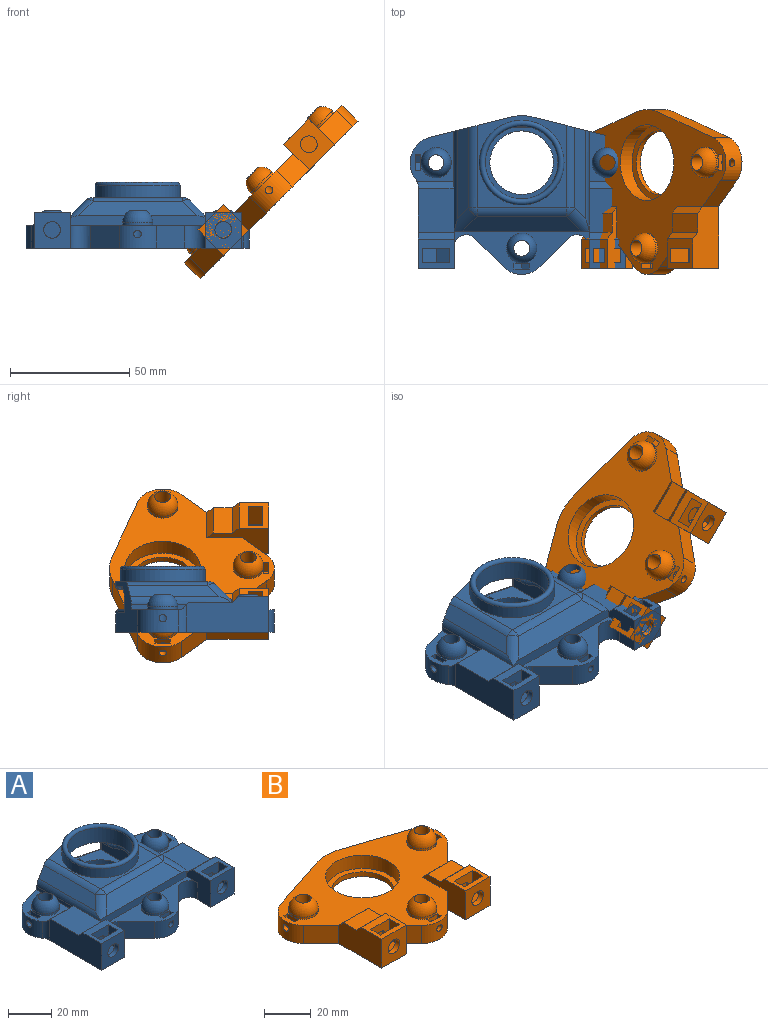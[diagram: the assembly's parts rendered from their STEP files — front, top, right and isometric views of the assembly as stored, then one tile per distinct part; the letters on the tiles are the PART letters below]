
ASSEMBLY  parts=2 mates=1
PART A: 137 faces, bbox 94x68.5x27.9 mm
  f0: plane 56.57x18.14mm, normal (0,0,1), area 376.9mm2, adj f1,f16,f17,f18,f32,f33,f34,f35
  f1: plane 56.98x4.44mm, normal (0,-1,0), area 230.6mm2, adj f0,f2,f5,f64,f65,f110,f113,f118
  f2: cylinder r=5.08mm len=42.23mm, axis (0,1,0), area 145.4mm2, adj f1,f22,f65,f68,f96,f111,f113
  f3: plane 21.1x18.45mm, normal (0,0,1), area 182.4mm2, adj f4,f11,f13,f40,f41,f42,f43,f52
  f4: plane 23.11x2.01mm, normal (-1,0,0), area 44.4mm2, adj f3,f5,f13,f69
  f5: cylinder r=5.08mm len=42.23mm, axis (0,-1,0), area 145.4mm2, adj f1,f4,f13,f64,f69,f109,f118
  f6: plane 22.5x8.14mm, normal (0,0,-1), area 85.2mm2, adj f100,f103,f108,f122,f124,f126
  f7: plane 34.42x31.06mm, normal (0,0,1), area 448.5mm2, adj f25,f28,f29,f30,f31,f95,f97,f98
  f8: plane 15.14x12.4mm, normal (0,0,1), area 120.2mm2, adj f14,f15,f67,f75,f76,f77,f78,f133
  f9: plane 15.14x12.4mm, normal (0,0,1), area 120.2mm2, adj f19,f20,f66,f70,f71,f72,f73,f136
  f10: plane 21.1x18.45mm, normal (0,0,1), area 182.4mm2, adj f21,f22,f36,f37,f38,f39,f53,f68
  f11: cylinder r=10.92mm len=17.33mm, axis (0,0,-1), area 199mm2, adj f3,f13,f27,f61,f91
  f12: cylinder r=3.3mm len=15.88mm, axis (0,0,-1), area 321.2mm2, adj f27,f57,f60
  f13: plane 33.96x21.44mm, normal (-0.24,0.97,0), area 452.5mm2, adj f3,f4,f5,f11,f26,f27,f99,f101
  f14: plane 34.54x15.19mm, normal (-1,0,0), area 465.8mm2, adj f8,f15,f27,f64,f67,f69,f91
  f15: plane 15.19x15.14mm, normal (0,-1,0), area 191.3mm2, adj f8,f14,f27,f83,f133
  f16: plane 11.93x11.93mm, normal (-0.71,-0.71,0), area 160.7mm2, adj f0,f17,f27,f89
  f17: cylinder r=10.92mm len=15.45mm, axis (0,0,-1), area 155.5mm2, adj f0,f16,f18,f27,f62
  f18: plane 11.93x11.93mm, normal (0.71,-0.71,0), area 160.7mm2, adj f0,f17,f27,f90
  f19: plane 15.19x15.14mm, normal (0,-1,0), area 191.3mm2, adj f9,f20,f27,f86,f136
  f20: plane 34.54x15.19mm, normal (1,0,0), area 465.8mm2, adj f9,f19,f27,f65,f66,f68,f92
  f21: cylinder r=10.92mm len=17.33mm, axis (0,0,-1), area 199mm2, adj f10,f22,f27,f59,f92
  f22: plane 33.96x21.44mm, normal (0.24,0.97,0), area 452.5mm2, adj f2,f10,f21,f26,f27,f96,f99,f101
  f23: cylinder r=3.3mm len=15.88mm, axis (0,0,-1), area 322.7mm2, adj f27,f55,f58
  f24: cylinder r=3.3mm len=15.88mm, axis (0,0,-1), area 321.2mm2, adj f27,f56,f63
  f25: cylinder r=13.33mm len=26.67mm, axis (0,0,-1), area 790.1mm2, adj f7,f27,f93
  f26: cylinder r=19.69mm len=9.6mm, axis (0,0,-1), area 72.2mm2, adj f13,f22,f27,f94,f123
  f27: plane 93.69x66.53mm, normal (0,0,-1), area 4184.5mm2, adj f11,f12,f13,f14,f15,f16,f17,f18
  f28: plane 5.46x2.34mm, normal (-1,0,0), area 12.8mm2, adj f7,f29,f31,f45
  f29: plane 7.32x6.45mm, normal (0,-1,0), area 33.3mm2, adj f7,f28,f30,f44,f45,f94
  f30: plane 5.46x2.34mm, normal (1,0,0), area 12.8mm2, adj f7,f29,f31,f44
  f31: plane 7.32x6.45mm, normal (0,1,0), area 33.3mm2, adj f7,f28,f30,f44,f45,f93
  f32: plane 7.32x6.45mm, normal (0,-1,0), area 33.3mm2, adj f0,f33,f35,f48,f49,f63
  f33: plane 5.46x2.34mm, normal (1,0,0), area 12.8mm2, adj f0,f32,f34,f49
  f34: plane 7.32x6.45mm, normal (0,1,0), area 33.3mm2, adj f0,f33,f35,f48,f49,f62
  f35: plane 5.46x2.34mm, normal (-1,0,0), area 12.8mm2, adj f0,f32,f34,f48
  f36: plane 5.46x2.34mm, normal (0,1,0), area 12.8mm2, adj f10,f37,f39,f47
  f37: plane 7.32x6.45mm, normal (-1,0,0), area 33.3mm2, adj f10,f36,f38,f46,f47,f59
  f38: plane 5.46x2.34mm, normal (0,-1,0), area 12.8mm2, adj f10,f37,f39,f46
  f39: plane 7.32x6.45mm, normal (1,0,0), area 33.3mm2, adj f10,f36,f38,f46,f47,f58
  f40: plane 5.46x2.34mm, normal (0,-1,0), area 12.8mm2, adj f3,f41,f43,f50
  f41: plane 7.32x6.45mm, normal (1,0,0), area 33.3mm2, adj f3,f40,f42,f50,f51,f61
  f42: plane 5.46x2.34mm, normal (0,1,0), area 12.8mm2, adj f3,f41,f43,f51
  f43: plane 7.32x6.45mm, normal (-1,0,0), area 33.3mm2, adj f3,f40,f42,f50,f51,f60
  f44: plane 3.23x2.34mm, normal (0.5,0,0.87), area 8.7mm2, adj f29,f30,f31,f45
  f45: plane 3.23x2.34mm, normal (-0.5,0,0.87), area 8.7mm2, adj f28,f29,f31,f44
  f46: plane 3.23x2.34mm, normal (0,-0.5,0.87), area 8.7mm2, adj f37,f38,f39,f47
  f47: plane 3.23x2.34mm, normal (0,0.5,0.87), area 8.7mm2, adj f36,f37,f39,f46
  f48: plane 3.23x2.34mm, normal (-0.5,0,0.87), area 8.7mm2, adj f32,f34,f35,f49
  f49: plane 3.23x2.34mm, normal (0.5,0,0.87), area 8.7mm2, adj f32,f33,f34,f48
  f50: plane 3.23x2.34mm, normal (0,-0.5,0.87), area 8.7mm2, adj f40,f41,f43,f51
  f51: plane 3.23x2.34mm, normal (0,0.5,0.87), area 8.7mm2, adj f41,f42,f43,f50
  f52: cylinder r=6.35mm len=12.7mm, axis (0,0,-1), area 42.7mm2, adj f3,f57
  f53: cylinder r=6.35mm len=12.7mm, axis (0,0,-1), area 42.7mm2, adj f10,f55
  f54: cylinder r=6.35mm len=12.7mm, axis (0,0,-1), area 42.7mm2, adj f0,f56
  f55: torus R=0.25mm, axis (0,0,1), area 212.4mm2, adj f23,f53
  f56: torus R=0.25mm, axis (0,0,1), area 212.4mm2, adj f24,f54
  f57: torus R=0.25mm, axis (0,0,1), area 212.4mm2, adj f12,f52
  f58: cylinder r=1.59mm len=3.49mm, axis (-1,0,0), area 31.5mm2, adj f23,f39
  f59: cylinder r=1.59mm len=3.18mm, axis (-1,0,0), area 21.1mm2, adj f21,f37
  f60: cylinder r=1.59mm len=3.18mm, axis (-1,0,0), area 30.4mm2, adj f12,f43
  f61: cylinder r=1.59mm len=3.18mm, axis (-1,0,0), area 22.3mm2, adj f11,f41
  f62: cylinder r=1.59mm len=3.18mm, axis (0,1,0), area 21.1mm2, adj f17,f34
  f63: cylinder r=1.59mm len=3.49mm, axis (0,1,0), area 34.8mm2, adj f24,f32
  f64: plane 18.44x15.14mm, normal (0,0,1), area 278.4mm2, adj f1,f5,f14,f67,f69,f133
  f65: plane 18.44x15.14mm, normal (0,0,1), area 278.4mm2, adj f1,f2,f20,f66,f68,f136
  f66: plane 15.14x2.82mm, normal (0,0.71,0.71), area 60.4mm2, adj f9,f20,f65,f136
  f67: plane 15.14x2.82mm, normal (0,0.71,0.71), area 60.4mm2, adj f8,f14,f64,f133
  f68: plane 15.52x2.88mm, normal (0,0.71,0.71), area 60.8mm2, adj f2,f10,f20,f65,f92,f96
  f69: plane 15.52x2.88mm, normal (0,0.71,0.71), area 60.8mm2, adj f3,f4,f5,f14,f64,f91
  f70: plane 14x11.25mm, normal (0,-1,0), area 100.6mm2, adj f9,f71,f73,f74,f79,f82,f87
  f71: plane 10.75x5.99mm, normal (1,0,0), area 64.5mm2, adj f9,f70,f72,f82
  f72: plane 14x11.25mm, normal (0,1,0), area 100.6mm2, adj f9,f71,f73,f74,f79,f82,f86
  f73: plane 10.74x5.99mm, normal (-1,0,0), area 64.4mm2, adj f9,f70,f72,f79
  f74: plane 5.99x0.01mm, normal (0,0,1), area 0mm2, adj f70,f72,f79,f82
  f75: plane 13.99x11.25mm, normal (0,-1,0), area 100.6mm2, adj f8,f76,f78,f80,f81,f84
  f76: plane 10.74x5.99mm, normal (1,0,0), area 64.4mm2, adj f8,f75,f77,f81
  f77: plane 13.99x11.25mm, normal (0,1,0), area 100.6mm2, adj f8,f76,f78,f80,f81,f83
  f78: plane 10.74x5.99mm, normal (-1,0,0), area 64.4mm2, adj f8,f75,f77,f80
  f79: plane 5.99x5.63mm, normal (-0.5,0,0.87), area 39mm2, adj f70,f72,f73,f74
  f80: plane 5.99x5.63mm, normal (-0.5,0,0.87), area 38.9mm2, adj f75,f77,f78,f81
  f81: plane 5.99x5.63mm, normal (0.5,0,0.87), area 38.9mm2, adj f75,f76,f77,f80
  f82: plane 5.99x5.61mm, normal (0.5,0,0.87), area 38.9mm2, adj f70,f71,f72,f74
  f83: cylinder r=3.51mm len=7.01mm, axis (0,1,0), area 54.8mm2, adj f15,f77
  f84: cylinder r=3.51mm len=7.01mm, axis (0,1,0), area 35.8mm2, adj f75,f85
  f85: plane 7.01x7.01mm, normal (0,-1,0), area 38.6mm2, adj f84
  f86: cylinder r=3.51mm len=7.01mm, axis (0,1,0), area 54.8mm2, adj f19,f72
  f87: cylinder r=3.51mm len=7.01mm, axis (0,1,0), area 35.8mm2, adj f70,f88
  f88: plane 7.01x7.01mm, normal (0,-1,0), area 38.6mm2, adj f87
  f89: cylinder r=5.13mm len=9.53mm, axis (0,0,1), area 115.1mm2, adj f0,f16,f27,f131,f132
  f90: cylinder r=5.13mm len=9.53mm, axis (0,0,1), area 115.1mm2, adj f0,f18,f27,f134,f135
  f91: cylinder r=5.13mm len=11.49mm, axis (0,0,-1), area 34.5mm2, adj f3,f11,f14,f27,f69
  f92: cylinder r=5.13mm len=11.49mm, axis (0,0,-1), area 34.5mm2, adj f10,f20,f21,f27,f68
  f93: cylinder r=1.59mm len=3.18mm, axis (0,1,0), area 13.7mm2, adj f25,f31
  f94: cylinder r=1.59mm len=3.18mm, axis (0,1,0), area 26.7mm2, adj f26,f29
  f95: plane 30.77x7.12mm, normal (1,0,0), area 158.5mm2, adj f7,f98,f106,f107,f108,f127
  f96: plane 23.11x2.01mm, normal (1,0,0), area 44.4mm2, adj f2,f10,f22,f68
  f97: plane 30.77x7.12mm, normal (-1,0,0), area 158.5mm2, adj f7,f98,f103,f104,f105,f119
  f98: plane 30.99x8.56mm, normal (0,1,0), area 257.5mm2, adj f7,f95,f97,f102,f105,f106
  f99: cylinder r=19.69mm len=9.6mm, axis (0,0,-1), area 18.5mm2, adj f13,f22,f101,f124
  f100: cylinder r=15.24mm len=30.48mm, axis (0,0,-1), area 790.5mm2, adj f6,f102,f104,f107,f130
  f101: plane 38.66x37.35mm, normal (0,0,1), area 384mm2, adj f13,f22,f99,f112,f115,f116,f129
  f102: plane 22.5x5.72mm, normal (0,0,-1), area 51.5mm2, adj f98,f100,f105,f106
  f103: cylinder r=4.24mm len=5.88mm, axis (0,1,0), area 34.6mm2, adj f6,f97,f104,f120
  f104: bspline ~20.56x4.24mm, area 73.7mm2, adj f97,f100,f103,f105
  f105: cylinder r=4.24mm len=5.72mm, axis (0,1,0), area 38.1mm2, adj f97,f98,f102,f104
  f106: cylinder r=4.24mm len=5.72mm, axis (0,-1,0), area 38.1mm2, adj f95,f98,f102,f107
  f107: bspline ~20.56x4.24mm, area 73.7mm2, adj f95,f100,f106,f108
  f108: cylinder r=4.24mm len=5.88mm, axis (0,-1,0), area 34.6mm2, adj f6,f95,f107,f128
  f109: plane 38.32x4.64mm, normal (-0.71,0,0.71), area 232.6mm2, adj f5,f13,f115,f118
  f110: plane 49.61x6.13mm, normal (0,-0.71,0.71), area 377mm2, adj f1,f113,f116,f118
  f111: plane 38.32x4.64mm, normal (0.71,0,0.71), area 232.6mm2, adj f2,f22,f112,f113
  f112: cylinder r=5.08mm len=34.58mm, axis (0,1,0), area 136.2mm2, adj f22,f101,f111,f114
  f113: cylinder r=5.08mm len=11.17mm, axis (0.58,-0.58,-0.58), area 59.6mm2, adj f1,f2,f110,f111,f114
  f114: sphere r=5.08mm, area 8.8mm2, adj f112,f113,f116
  f115: cylinder r=5.08mm len=34.58mm, axis (0,-1,0), area 136.2mm2, adj f13,f101,f109,f117
  f116: cylinder r=5.08mm len=37.35mm, axis (1,0,0), area 149mm2, adj f101,f110,f114,f117
  f117: sphere r=5.08mm, area 11.9mm2, adj f115,f116,f118
  f118: cylinder r=5.08mm len=11.17mm, axis (-0.58,-0.58,-0.58), area 59.6mm2, adj f1,f5,f109,f110,f117
  f119: cylinder r=1.27mm len=5.59mm, axis (0,0,-1), area 10.9mm2, adj f7,f22,f97,f120,f121
  f120: bspline ~6.01x5.75mm, area 16.3mm2, adj f22,f103,f119,f122
  f121: cylinder r=1.27mm len=12.58mm, axis (0.97,-0.24,0), area 24mm2, adj f7,f22,f119,f123
  f122: cylinder r=1.27mm len=7.07mm, axis (-0.97,0.24,0), area 13.9mm2, adj f6,f22,f120,f124
  f123: torus R=18.41mm, axis (0,0,1), area 18.9mm2, adj f7,f26,f121,f125
  f124: torus R=18.41mm, axis (0,0,1), area 18.9mm2, adj f6,f99,f122,f126
  f125: cylinder r=1.27mm len=12.58mm, axis (0.97,0.24,0), area 24mm2, adj f7,f13,f123,f127
  f126: cylinder r=1.27mm len=7.07mm, axis (-0.97,-0.24,0), area 13.9mm2, adj f6,f13,f124,f128
  f127: cylinder r=1.27mm len=5.59mm, axis (0,0,-1), area 10.9mm2, adj f7,f13,f95,f125,f128
  f128: bspline ~6.01x5.51mm, area 16.3mm2, adj f13,f108,f126,f127
  f129: cylinder r=17.78mm len=35.56mm, axis (0,0,-1), area 567.5mm2, adj f101,f130
  f130: torus R=16.51mm, axis (0,0,1), area 413.9mm2, adj f100,f129
  f131: plane 9.53x0.13mm, normal (0,1,0), area 1.2mm2, adj f27,f89,f132,f133
  f132: plane 1.13x0.13mm, normal (0,0,-1), area 0.1mm2, adj f89,f131,f133
  f133: plane 15.75x15.19mm, normal (1,0,0), area 170.5mm2, adj f0,f1,f8,f15,f27,f64,f67,f131
  f134: plane 1.13x0.13mm, normal (0,0,-1), area 0.1mm2, adj f90,f135,f136
  f135: plane 9.53x0.13mm, normal (0,1,0), area 1.2mm2, adj f27,f90,f134,f136
  f136: plane 15.75x15.19mm, normal (-1,0,0), area 170.5mm2, adj f0,f1,f9,f19,f27,f65,f66,f134
PART B: 81 faces, bbox 93.7x69.1x15.9 mm
  f0: plane 15.01x12.4mm, normal (0,0,1), area 118.6mm2, adj f7,f8,f9,f59,f67,f68,f69,f70
  f1: plane 15.01x12.4mm, normal (0,0,1), area 118.6mm2, adj f13,f14,f15,f58,f62,f63,f64,f65
  f2: plane 93.69x69.07mm, normal (0,0,1), area 2582.6mm2, adj f3,f5,f6,f9,f10,f11,f12,f13
  f3: cylinder r=10.92mm len=18.09mm, axis (0,0,-1), area 203.9mm2, adj f2,f5,f6,f23,f53
  f4: cylinder r=3.3mm len=15.88mm, axis (0,0,-1), area 321.2mm2, adj f23,f49,f52
  f5: plane 32.36x10.73mm, normal (-0.31,0.95,0), area 324.8mm2, adj f2,f3,f22,f23
  f6: plane 10.74x10.74mm, normal (-0.71,-0.71,0), area 144.7mm2, adj f2,f3,f7,f23
  f7: plane 25.99x15.19mm, normal (-1,0,0), area 356.3mm2, adj f0,f6,f8,f23,f56,f59,f61
  f8: plane 15.19x15.01mm, normal (0,-1,0), area 189.4mm2, adj f0,f7,f9,f23,f75
  f9: plane 25.99x15.19mm, normal (1,0,0), area 213.4mm2, adj f0,f2,f8,f10,f23,f56,f59,f61
  f10: plane 10.17x10.17mm, normal (-0.71,-0.71,0), area 137mm2, adj f2,f9,f11,f23
  f11: cylinder r=10.92mm len=15.45mm, axis (0,0,-1), area 155.5mm2, adj f2,f10,f12,f23,f54
  f12: plane 10.17x10.17mm, normal (0.71,-0.71,0), area 137mm2, adj f2,f11,f13,f23
  f13: plane 25.99x15.19mm, normal (-1,0,0), area 213.4mm2, adj f1,f2,f12,f14,f23,f57,f58,f60
  f14: plane 15.19x15.01mm, normal (0,-1,0), area 189.4mm2, adj f1,f13,f15,f23,f78
  f15: plane 25.99x15.19mm, normal (1,0,0), area 356.3mm2, adj f1,f14,f16,f23,f57,f58,f60
  f16: plane 10.74x10.74mm, normal (0.71,-0.71,0), area 144.7mm2, adj f2,f15,f17,f23
  f17: cylinder r=10.92mm len=18.09mm, axis (0,0,-1), area 203.9mm2, adj f2,f16,f18,f23,f51
  f18: plane 32.36x10.73mm, normal (0.31,0.95,0), area 324.8mm2, adj f2,f17,f22,f23
  f19: cylinder r=3.3mm len=15.88mm, axis (0,0,-1), area 321.2mm2, adj f23,f47,f50
  f20: cylinder r=3.3mm len=15.88mm, axis (0,0,-1), area 321.2mm2, adj f23,f48,f55
  f21: cylinder r=15.88mm len=31.75mm, axis (0,0,-1), area 696.7mm2, adj f2,f25
  f22: cylinder r=22.23mm len=13.99mm, axis (0,0,-1), area 135.5mm2, adj f2,f5,f18,f23
  f23: plane 93.69x69.07mm, normal (0,0,-1), area 3918.4mm2, adj f3,f4,f5,f6,f7,f8,f9,f10
  f24: cylinder r=13.33mm len=26.67mm, axis (0,0,-1), area 212.8mm2, adj f23,f25
  f25: plane 31.75x31.75mm, normal (0,0,1), area 233.1mm2, adj f21,f24
  f26: plane 7.32x6.45mm, normal (0,-1,0), area 33.3mm2, adj f2,f27,f29,f40,f41,f55
  f27: plane 5.46x2.34mm, normal (1,0,0), area 12.8mm2, adj f2,f26,f28,f41
  f28: plane 7.32x6.45mm, normal (0,1,0), area 33.3mm2, adj f2,f27,f29,f40,f41,f54
  f29: plane 5.46x2.34mm, normal (-1,0,0), area 12.8mm2, adj f2,f26,f28,f40
  f30: plane 5.46x2.34mm, normal (0,1,0), area 12.8mm2, adj f2,f31,f33,f39
  f31: plane 7.32x6.45mm, normal (-1,0,0), area 33.3mm2, adj f2,f30,f32,f38,f39,f51
  f32: plane 5.46x2.34mm, normal (0,-1,0), area 12.8mm2, adj f2,f31,f33,f38
  f33: plane 7.32x6.45mm, normal (1,0,0), area 33.3mm2, adj f2,f30,f32,f38,f39,f50
  f34: plane 5.46x2.34mm, normal (0,-1,0), area 12.8mm2, adj f2,f35,f37,f42
  f35: plane 7.32x6.45mm, normal (1,0,0), area 33.3mm2, adj f2,f34,f36,f42,f43,f53
  f36: plane 5.46x2.34mm, normal (0,1,0), area 12.8mm2, adj f2,f35,f37,f43
  f37: plane 7.32x6.45mm, normal (-1,0,0), area 33.3mm2, adj f2,f34,f36,f42,f43,f52
  f38: plane 3.23x2.34mm, normal (0,-0.5,0.87), area 8.7mm2, adj f31,f32,f33,f39
  f39: plane 3.23x2.34mm, normal (0,0.5,0.87), area 8.7mm2, adj f30,f31,f33,f38
  f40: plane 3.23x2.34mm, normal (-0.5,0,0.87), area 8.7mm2, adj f26,f28,f29,f41
  f41: plane 3.23x2.34mm, normal (0.5,0,0.87), area 8.7mm2, adj f26,f27,f28,f40
  f42: plane 3.23x2.34mm, normal (0,-0.5,0.87), area 8.7mm2, adj f34,f35,f37,f43
  f43: plane 3.23x2.34mm, normal (0,0.5,0.87), area 8.7mm2, adj f35,f36,f37,f42
  f44: cylinder r=6.35mm len=12.7mm, axis (0,0,-1), area 42.7mm2, adj f2,f49
  f45: cylinder r=6.35mm len=12.7mm, axis (0,0,-1), area 42.7mm2, adj f2,f47
  f46: cylinder r=6.35mm len=12.7mm, axis (0,0,-1), area 42.7mm2, adj f2,f48
  f47: torus R=0.25mm, axis (0,0,1), area 212.4mm2, adj f19,f45
  f48: torus R=0.25mm, axis (0,0,1), area 212.4mm2, adj f20,f46
  f49: torus R=0.25mm, axis (0,0,1), area 212.4mm2, adj f4,f44
  f50: cylinder r=1.59mm len=3.49mm, axis (-1,0,0), area 32.4mm2, adj f19,f33
  f51: cylinder r=1.59mm len=3.18mm, axis (-1,0,0), area 21.7mm2, adj f17,f31
  f52: cylinder r=1.59mm len=3.49mm, axis (-1,0,0), area 32.4mm2, adj f4,f37
  f53: cylinder r=1.59mm len=3.18mm, axis (-1,0,0), area 21.7mm2, adj f3,f35
  f54: cylinder r=1.59mm len=3.18mm, axis (0,1,0), area 21.7mm2, adj f11,f28
  f55: cylinder r=1.59mm len=3.49mm, axis (0,1,0), area 32.4mm2, adj f20,f26
  f56: plane 15.01x7.93mm, normal (0,0,1), area 119mm2, adj f7,f9,f59,f61
  f57: plane 15.01x7.93mm, normal (0,0,1), area 119mm2, adj f13,f15,f58,f60
  f58: plane 15.01x2.82mm, normal (0,0.71,0.71), area 59.9mm2, adj f1,f13,f15,f57
  f59: plane 15.01x2.82mm, normal (0,0.71,0.71), area 59.9mm2, adj f0,f7,f9,f56
  f60: plane 15.01x2.84mm, normal (0,0.71,0.71), area 60.4mm2, adj f2,f13,f15,f57
  f61: plane 15.01x2.84mm, normal (0,0.71,0.71), area 60.4mm2, adj f2,f7,f9,f56
  f62: plane 14x11.25mm, normal (0,-1,0), area 100.6mm2, adj f1,f63,f65,f66,f71,f74,f79
  f63: plane 10.75x5.99mm, normal (1,0,0), area 64.5mm2, adj f1,f62,f64,f74
  f64: plane 14x11.25mm, normal (0,1,0), area 100.6mm2, adj f1,f63,f65,f66,f71,f74,f78
  f65: plane 10.74x5.99mm, normal (-1,0,0), area 64.4mm2, adj f1,f62,f64,f71
  f66: plane 5.99x0.01mm, normal (0,0,1), area 0mm2, adj f62,f64,f71,f74
  f67: plane 13.99x11.25mm, normal (0,-1,0), area 100.6mm2, adj f0,f68,f70,f72,f73,f76
  f68: plane 10.74x5.99mm, normal (1,0,0), area 64.4mm2, adj f0,f67,f69,f73
  f69: plane 13.99x11.25mm, normal (0,1,0), area 100.6mm2, adj f0,f68,f70,f72,f73,f75
  f70: plane 10.74x5.99mm, normal (-1,0,0), area 64.4mm2, adj f0,f67,f69,f72
  f71: plane 5.99x5.63mm, normal (-0.5,0,0.87), area 39mm2, adj f62,f64,f65,f66
  f72: plane 5.99x5.63mm, normal (-0.5,0,0.87), area 38.9mm2, adj f67,f69,f70,f73
  f73: plane 5.99x5.63mm, normal (0.5,0,0.87), area 38.9mm2, adj f67,f68,f69,f72
  f74: plane 5.99x5.61mm, normal (0.5,0,0.87), area 38.9mm2, adj f62,f63,f64,f66
  f75: cylinder r=3.51mm len=7.01mm, axis (0,1,0), area 54.8mm2, adj f8,f69
  f76: cylinder r=3.51mm len=7.01mm, axis (0,1,0), area 35.8mm2, adj f67,f77
  f77: plane 7.01x7.01mm, normal (0,-1,0), area 38.6mm2, adj f76
  f78: cylinder r=3.51mm len=7.01mm, axis (0,1,0), area 54.8mm2, adj f14,f64
  f79: cylinder r=3.51mm len=7.01mm, axis (0,1,0), area 35.8mm2, adj f62,f80
  f80: plane 7.01x7.01mm, normal (0,-1,0), area 38.6mm2, adj f79
PLACE A t=(-69.67,15.82,4.71)mm
PLACE B rot(axis=(0,-1,0),45deg) t=(-10.36,15.82,24.93)mm
MATE revolute B.f75 <-> A.f86  axis (0,-1,0) through (-33.76,7.29,12.41)mm
